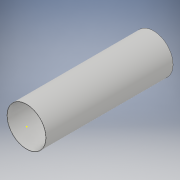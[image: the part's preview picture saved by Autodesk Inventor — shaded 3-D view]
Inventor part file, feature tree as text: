
AUTODESK INVENTOR PART (.ipt)
format: ipt  version: 2019 (Build 230136000, 136)  size: 99,328 bytes
history: native  units: mm
features: sketch x3, extrude x2
ambient origin geometry x8: Origin, YZ Plane, XZ Plane, XY Plane, X Axis, Y Axis, Z Axis, Center Point
bodies: Solid1 (feature_tree)
feature tree (5):
  extrude  "Extrusion1"  Depth=202.545mm TaperAngle=0.0deg
  sketch  "Sketch2"  dims[d3=61.5mm d4=202.545mm d5=0.0mm]
  extrude  "Extrusion2"  Depth=202.545mm TaperAngle=0.0deg
  sketch  "Sketch1"  dims[d0=62.48mm d1=202.545mm d2=0.0mm]
  sketch  "Sketch3"
